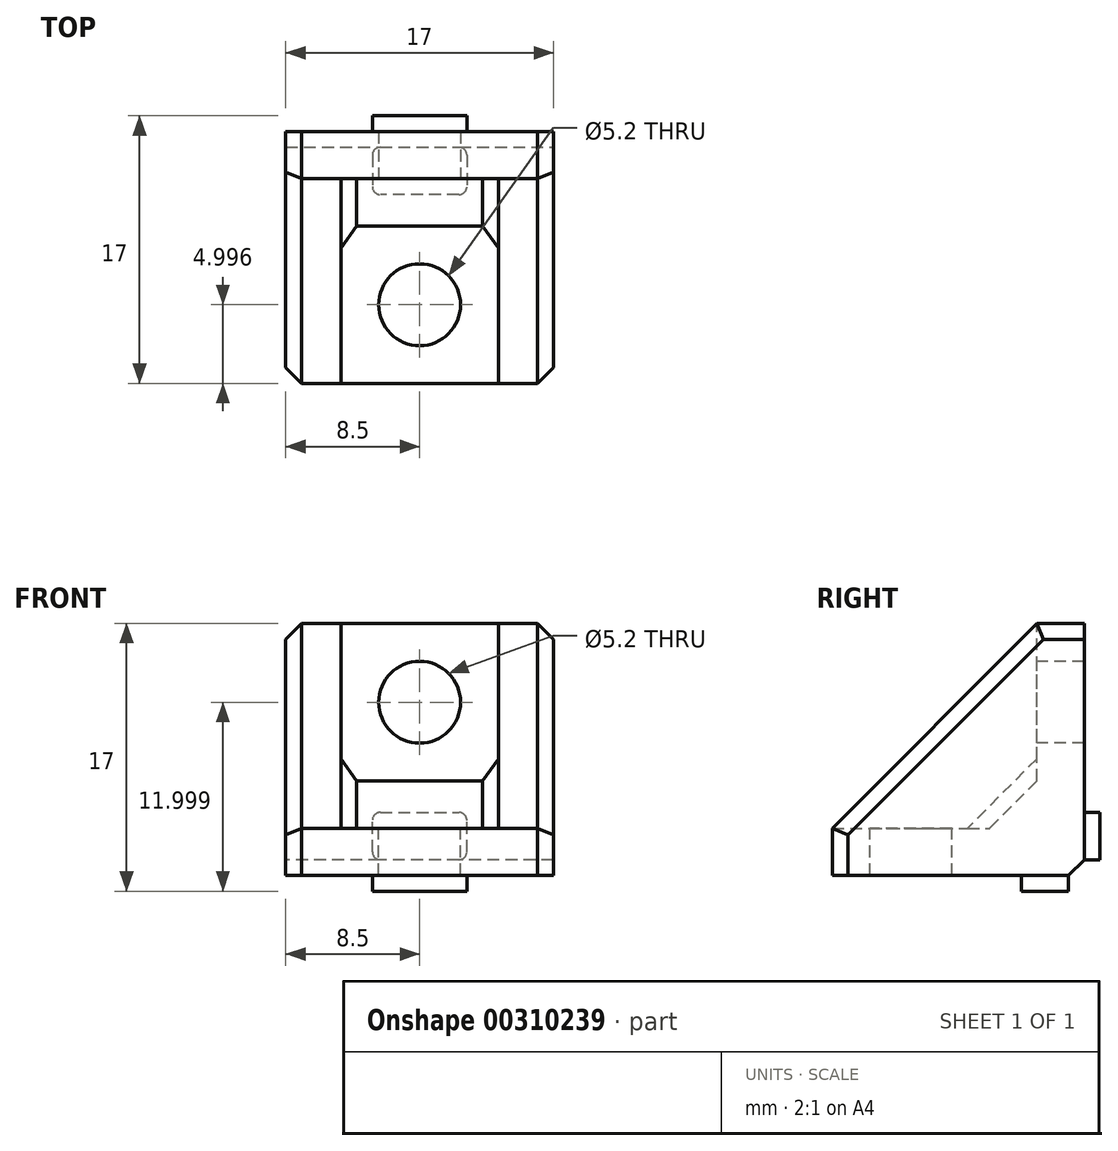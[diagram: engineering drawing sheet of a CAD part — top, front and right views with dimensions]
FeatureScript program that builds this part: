
annotation { "Feature Type Name" : "Feature", "Feature Type Description" : "" }
export const myFeature = defineFeature(function(context is Context, id is Id, definition is map)
    precondition{}
    {
        {
            var Q0;
            Q0=qCreatedBy(makeId("Right.planeOp"),FACE);
            var sketch = newSketch(context, id + "F0", { "sketchPlane" : qUnion([Q0])});
            skLineSegment(sketch, "E0", {"start": v(-0.33, -1.01) * mm, "end": v(15.67, -1.01) * mm});
            skLineSegment(sketch, "E1", {"start": v(15.67, -1.01) * mm, "end": v(15.67, 14.99) * mm});
            skLineSegment(sketch, "E2", {"start": v(15.67, 14.99) * mm, "end": v(12.67, 14.99) * mm});
            skLineSegment(sketch, "E3", {"start": v(-0.33, -1.01) * mm, "end": v(-0.33, 1.99) * mm});
            skLineSegment(sketch, "E4", {"start": v(-0.33, 1.99) * mm, "end": v(12.67, 14.99) * mm});
            skLineSegment(sketch, "E5", {"start": v(-0.33, 1.99) * mm, "end": v(9.67, 1.99) * mm});
            skLineSegment(sketch, "E6", {"start": v(9.67, 1.99) * mm, "end": v(12.67, 4.99) * mm});
            skLineSegment(sketch, "E7", {"start": v(12.67, 4.99) * mm, "end": v(12.67, 14.99) * mm});
            skSolve(sketch);
        }
        {
            var Q0;
            Q0=makeQuery(id+"F0.imprint","IMPRINT",FACE,{"disambiguationData":[TD([[makeQuery(id+"F0.imprint","IMPRINT",EDGE,{"derivedFrom":sQuery(id+"F0.wireOp",EDGE,"E0")}),1.0]])]});
            var Q1;
            Q1=makeQuery(id+"F0.imprint","IMPRINT",FACE,{"disambiguationData":[TD([[makeQuery(id+"F0.imprint","IMPRINT",EDGE,{"derivedFrom":sQuery(id+"F0.wireOp",EDGE,"E4")}),-1.0]])]});
            extrude(context, id + "F1", {"entities" : qUnion([Q0, Q1]), "endBound" : BoundingType.SYMMETRIC, "depth" : 17 * mm});
        }
        {
            var Q0;
            Q0=makeQuery(id+"F0.imprint","IMPRINT",FACE,{"disambiguationData":[TD([[makeQuery(id+"F0.imprint","IMPRINT",EDGE,{"derivedFrom":sQuery(id+"F0.wireOp",EDGE,"E4")}),-1.0]])]});
            extrude(context, id + "F2", {"entities" : qUnion([Q0]), "operationType" : NewBodyOperationType.REMOVE, "endBound" : BoundingType.SYMMETRIC, "depth" : 10 * mm});
        }
        {
            var Q0;
            Q0=makeQuery(id+"F2.boolean.opBoolean","COPY",FACE,{"derivedFrom":makeQuery(id+"F2.opExtrude","SWEPT_FACE",FACE,{"disambiguationData":[OSD([sQuery(id+"F0.wireOp",EDGE,"E7")])]})});
            var sketch = newSketch(context, id + "F3", { "sketchPlane" : qUnion([Q0])});
            skCircle(sketch, "E8", {"center": v(0, 9.99) * mm, "radius": 2.6 * mm});
            skSolve(sketch);
        }
        {
            var Q0;
            Q0=makeQuery(id+"F3.imprint","IMPRINT",FACE,{"disambiguationData":[TD([[makeQuery(id+"F3.imprint","IMPRINT",EDGE,{"derivedFrom":sQuery(id+"F3.wireOp",EDGE,"E8")}),1.0]])]});
            extrude(context, id + "F4", {"entities" : qUnion([Q0]), "operationType" : NewBodyOperationType.REMOVE, "oppositeDirection" : true, "depth" : 25 * mm});
        }
        {
            var Q0;
            Q0=makeQuery(id+"F2.boolean.opBoolean","COPY",FACE,{"derivedFrom":makeQuery(id+"F2.opExtrude","SWEPT_FACE",FACE,{"disambiguationData":[OSD([sQuery(id+"F0.wireOp",EDGE,"E5")])]})});
            var sketch = newSketch(context, id + "F5", { "sketchPlane" : qUnion([Q0])});
            skCircle(sketch, "E9", {"center": v(0, 4.67) * mm, "radius": 2.6 * mm});
            skSolve(sketch);
        }
        {
            var Q0;
            Q0=makeQuery(id+"F5.imprint","IMPRINT",FACE,{"disambiguationData":[TD([[makeQuery(id+"F5.imprint","IMPRINT",EDGE,{"derivedFrom":sQuery(id+"F5.wireOp",EDGE,"E9")}),1.0]])]});
            extrude(context, id + "F6", {"entities" : qUnion([Q0]), "operationType" : NewBodyOperationType.REMOVE, "oppositeDirection" : true, "depth" : 25 * mm});
        }
        {
            var Q0;
            Q0=makeQuery(id+"F1.opExtrude","CAP_EDGE",EDGE,{"disambiguationData":[OSD([sQuery(id+"F0.wireOp",EDGE,"E2")])],"isStart":true});
            var Q1;
            Q1=makeQuery(id+"F1.opExtrude","CAP_EDGE",EDGE,{"disambiguationData":[OSD([sQuery(id+"F0.wireOp",EDGE,"E4")])],"isStart":true});
            var Q2;
            Q2=makeQuery(id+"F1.opExtrude","CAP_EDGE",EDGE,{"disambiguationData":[OSD([sQuery(id+"F0.wireOp",EDGE,"E3")])],"isStart":true});
            var Q3;
            Q3=makeQuery(id+"F1.opExtrude","CAP_EDGE",EDGE,{"disambiguationData":[OSD([sQuery(id+"F0.wireOp",EDGE,"E3")])],"isStart":false});
            var Q4;
            Q4=makeQuery(id+"F1.opExtrude","CAP_EDGE",EDGE,{"disambiguationData":[OSD([sQuery(id+"F0.wireOp",EDGE,"E4")])],"isStart":false});
            var Q5;
            Q5=makeQuery(id+"F1.opExtrude","CAP_EDGE",EDGE,{"disambiguationData":[OSD([sQuery(id+"F0.wireOp",EDGE,"E2")])],"isStart":false});
            var Q6;
            Q6=makeQuery(id+"F2.boolean.opBoolean","COPY",EDGE,{"derivedFrom":makeQuery(id+"F2.opExtrude","CAP_EDGE",EDGE,{"disambiguationData":[OSD([sQuery(id+"F0.wireOp",EDGE,"E6")])],"isStart":true})});
            var Q7;
            Q7=makeQuery(id+"F2.boolean.opBoolean","COPY",EDGE,{"derivedFrom":makeQuery(id+"F2.opExtrude","CAP_EDGE",EDGE,{"disambiguationData":[OSD([sQuery(id+"F0.wireOp",EDGE,"E6")])],"isStart":false})});
            var Q8;
            Q8=makeQuery(id+"F1.opExtrude","SWEPT_EDGE",EDGE,{"disambiguationData":[OSD([sQuery(id+"F0.wireOp",EDGE,"E0"),sQuery(id+"F0.wireOp",EDGE,"E1")])]});
            chamfer(context, id + "F7", {"entities" : qUnion([Q0, Q1, Q2, Q3, Q4, Q5, Q6, Q7, Q8]), "width" : 1 * mm, "tangentPropagation" : true});
        }
        {
            var Q0;
            Q0=makeQuery(id+"F1.opExtrude","SWEPT_FACE",FACE,{"disambiguationData":[OSD([sQuery(id+"F0.wireOp",EDGE,"E1")])]});
            var sketch = newSketch(context, id + "F8", { "sketchPlane" : qUnion([Q0])});
            skLineSegment(sketch, "E10.bottom", {"start": v(3, -0.01) * mm, "end": v(-3, -0.01) * mm});
            skLineSegment(sketch, "E10.top", {"start": v(3, 2.99) * mm, "end": v(-3, 2.99) * mm});
            skLineSegment(sketch, "E10.left", {"start": v(3, -0.01) * mm, "end": v(3, 2.99) * mm});
            skLineSegment(sketch, "E10.right", {"start": v(-3, -0.01) * mm, "end": v(-3, 2.99) * mm});
            skPoint(sketch, "E10.middle", {"position": v(0, 1.49) * mm});
            skSolve(sketch);
        }
        {
            var Q0;
            Q0=makeQuery(id+"F8.imprint","IMPRINT",FACE,{"disambiguationData":[TD([[makeQuery(id+"F8.imprint","IMPRINT",EDGE,{"derivedFrom":sQuery(id+"F8.wireOp",EDGE,"E10.bottom")}),1.0]])]});
            extrude(context, id + "F9", {"entities" : qUnion([Q0]), "operationType" : NewBodyOperationType.ADD, "depth" : 1 * mm});
        }
        {
            var Q0;
            Q0=makeQuery(id+"F1.opExtrude","SWEPT_FACE",FACE,{"disambiguationData":[OSD([sQuery(id+"F0.wireOp",EDGE,"E0")])]});
            var sketch = newSketch(context, id + "F10", { "sketchPlane" : qUnion([Q0])});
            skLineSegment(sketch, "E11.bottom", {"start": v(3, -14.67) * mm, "end": v(-3, -14.67) * mm});
            skLineSegment(sketch, "E11.top", {"start": v(3, -11.67) * mm, "end": v(-3, -11.67) * mm});
            skLineSegment(sketch, "E11.left", {"start": v(3, -14.67) * mm, "end": v(3, -11.67) * mm});
            skLineSegment(sketch, "E11.right", {"start": v(-3, -14.67) * mm, "end": v(-3, -11.67) * mm});
            skPoint(sketch, "E11.middle", {"position": v(0, -13.17) * mm});
            skSolve(sketch);
        }
        {
            var Q0;
            Q0=makeQuery(id+"F10.imprint","IMPRINT",FACE,{"disambiguationData":[TD([[makeQuery(id+"F10.imprint","IMPRINT",EDGE,{"derivedFrom":sQuery(id+"F10.wireOp",EDGE,"E11.bottom")}),1.0]])]});
            extrude(context, id + "F11", {"entities" : qUnion([Q0]), "operationType" : NewBodyOperationType.ADD, "depth" : 1 * mm});
        }
        {
            var Q0;
            Q0=makeQuery(id+"F9.opExtrude","SWEPT_EDGE",EDGE,{"disambiguationData":[OSD([sQuery(id+"F8.wireOp",EDGE,"E10.top"),sQuery(id+"F8.wireOp",EDGE,"E10.right")])]});
            var Q1;
            Q1=makeQuery(id+"F9.opExtrude","SWEPT_EDGE",EDGE,{"disambiguationData":[OSD([sQuery(id+"F0.wireOp",EDGE,"E0"),sQuery(id+"F0.wireOp",EDGE,"E1"),sQuery(id+"F8.wireOp",EDGE,"E10.bottom"),sQuery(id+"F8.wireOp",EDGE,"E10.right")])]});
            var Q2;
            Q2=makeQuery(id+"F9.opExtrude","SWEPT_EDGE",EDGE,{"disambiguationData":[OSD([sQuery(id+"F8.wireOp",EDGE,"E10.top"),sQuery(id+"F8.wireOp",EDGE,"E10.left")])]});
            var Q3;
            Q3=makeQuery(id+"F9.opExtrude","SWEPT_EDGE",EDGE,{"disambiguationData":[OSD([sQuery(id+"F0.wireOp",EDGE,"E0"),sQuery(id+"F0.wireOp",EDGE,"E1"),sQuery(id+"F8.wireOp",EDGE,"E10.bottom"),sQuery(id+"F8.wireOp",EDGE,"E10.left")])]});
            var Q4;
            Q4=makeQuery(id+"F11.opExtrude","SWEPT_EDGE",EDGE,{"disambiguationData":[OSD([sQuery(id+"F10.wireOp",EDGE,"E11.top"),sQuery(id+"F10.wireOp",EDGE,"E11.right")])]});
            var Q5;
            Q5=makeQuery(id+"F11.opExtrude","SWEPT_EDGE",EDGE,{"disambiguationData":[OSD([sQuery(id+"F0.wireOp",EDGE,"E0"),sQuery(id+"F0.wireOp",EDGE,"E1"),sQuery(id+"F10.wireOp",EDGE,"E11.bottom"),sQuery(id+"F10.wireOp",EDGE,"E11.right")])]});
            var Q6;
            Q6=makeQuery(id+"F11.opExtrude","SWEPT_EDGE",EDGE,{"disambiguationData":[OSD([sQuery(id+"F10.wireOp",EDGE,"E11.top"),sQuery(id+"F10.wireOp",EDGE,"E11.left")])]});
            var Q7;
            Q7=makeQuery(id+"F11.opExtrude","SWEPT_EDGE",EDGE,{"disambiguationData":[OSD([sQuery(id+"F0.wireOp",EDGE,"E0"),sQuery(id+"F0.wireOp",EDGE,"E1"),sQuery(id+"F10.wireOp",EDGE,"E11.bottom"),sQuery(id+"F10.wireOp",EDGE,"E11.left")])]});
            fillet(context, id + "F12", {"entities" : qUnion([Q0, Q1, Q2, Q3, Q4, Q5, Q6, Q7]), "radius" : .5 * mm, "tangentPropagation" : true, "allowEdgeOverflow" : false});
        }
    });
